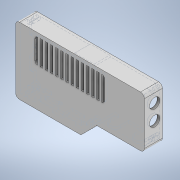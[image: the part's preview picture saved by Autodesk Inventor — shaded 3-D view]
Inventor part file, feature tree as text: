
AUTODESK INVENTOR PART (.ipt)
format: ipt  version: 2021 (Build 250183000, 183)  size: 515,072 bytes
history: native  units: mm
features: sketch x22, extrude x21, chamfer x5, fillet x3, hole x1
ambient origin geometry x8: Origin, YZ Plane, XZ Plane, XY Plane, X Axis, Y Axis, Z Axis, Center Point
bodies: Solid1 (feature_tree)
feature tree (52):
  extrude  "Extrusion1"  Depth=100.0mm
  extrude  "Extrusion3"  Depth=50.0mm
  extrude  "Extrusion4"  Depth=12.5mm
  extrude  "Extrusion12"  Depth=3.0mm TaperAngle=0.0deg
  extrude  "Extrusion13"  Depth=3.0mm TaperAngle=0.0deg
  fillet  "Fillet3"  Radius=2.0mm
  extrude  "Extrusion14"  Depth=2.0mm
  extrude  "Extrusion15"  Depth=44.0mm
  extrude  "Extrusion16"  Depth=12.0mm TaperAngle=0.0deg
  extrude  "Extrusion18"  Depth=12.6mm
  extrude  "Extrusion19"  Depth=3.0mm
  extrude  "Extrusion20"  Depth=1.5mm TaperAngle=0.0deg
  extrude  "Extrusion21"  Depth=4.4mm TaperAngle=0.0deg
  extrude  "Extrusion22"  Depth=2.0mm TaperAngle=0.0deg
  extrude  "Extrusion23"  Depth=14.0mm
  extrude  "Extrusion25"  Depth=4.4mm TaperAngle=0.0deg
  extrude  "Extrusion26"  Depth=4.0mm
  hole  "Hole2"  [1 undecoded]
  chamfer  "Chamfer3"  Distance=12.0mm
  chamfer  "Chamfer4"  Distance=12.0mm
  chamfer  "Chamfer5"  Distance=2.0mm
  chamfer  "Chamfer6"  Distance=8.0mm
  chamfer  "Chamfer7"  Distance=10.0mm
  extrude  "Extrusion27"  Depth=12.0mm
  fillet  "Fillet4"  Radius=8.0mm
  extrude  "Extrusion28"  Depth=8.0mm
  extrude  "Extrusion29"  Depth=8.0mm
  extrude  "Extrusion30"  Depth=2.0mm TaperAngle=0.0deg
  fillet  "Fillet5"  Radius=1.6mm
  extrude  "Extrusion31"  Depth=0.5mm
  sketch  "Sketch1"  dims[d0=52.0mm d1=100.0mm]
  sketch  "Sketch4"  dims[d2=26.0mm d3=50.0mm]
  sketch  "Sketch5"  dims[d4=2.0mm d5=0.0mm d35=12.5mm]
  sketch  "Sketch13"  dims[d36=63.1mm d37=3.0mm d38=0.0mm]
  sketch  "Sketch14"  dims[d39=50.673mm d40=3.0mm d41=0.0mm d79=2.0mm]
  sketch  "Sketch15"  dims[d80=2.0mm d81=2.0mm]
  sketch  "Sketch16"  dims[d82=1.2mm d83=44.0mm]
  sketch  "Sketch17"  dims[d84=59.0mm d85=12.0mm d86=0.0mm]
  sketch  "Sketch19"  dims[d87=2.0mm d88=12.6mm]
  sketch  "Sketch20"  dims[d89=12.0mm d90=0.0mm d91=3.0mm]
  sketch  "Sketch21"  dims[d92=7.8mm d93=1.5mm d94=0.0mm]
  sketch  "Sketch22"  dims[d95=33.8mm d96=4.4mm d97=0.0mm]
  sketch  "Sketch23"  dims[d98=2.0mm d99=2.0mm d100=0.0mm]
  sketch  "Sketch24"  dims[d108=3.0mm d109=14.0mm]
  sketch  "Sketch26"  dims[d110=10.0mm d111=4.4mm d112=0.0mm]
  sketch  "Sketch27"  dims[d113=1.3mm d114=4.0mm]
  sketch  "Sketch28"  dims[d115=3.0mm d116=0.0mm d117=2.0mm]
  sketch  "Sketch29"  dims[d118=2.0mm d119=12.0mm d120=0.0mm d121=12.0mm d122=0.0mm]
  sketch  "Sketch30"  dims[d123=70.0mm]
  sketch  "Sketch31"  dims[d124=89.0mm]
  sketch  "Sketch32"  dims[d125=8.0mm]
  sketch  "Sketch33"  dims[d126=8.0mm d127=2.0mm d128=0.0mm d129=8.0mm d130=10.0mm d131=12.0mm d132=8.0mm d133=8.0mm d134=8.0mm d135=2.0mm d136=0.0mm d140=1.6mm d141=0.5mm d142=9.4mm d143=0.0mm d144=3.0mm d145=3.0mm d146=3.0mm d147=50.0mm d148=97.0mm d149=15.0mm d150=3.0mm d151=3.0mm d152=97.0mm d153=49.0mm d154=4.8mm d155=4.8mm d156=4.8mm d157=4.8mm d158=4.8mm d159=5.0mm d160=0.0mm d161=2.0mm d162=6.0mm d163=4.0mm d164=2.0mm d165=90.0deg d166=4.0mm d167=20.594885mm d168=2.0mm d169=2.0mm d170=45.0deg d171=1.0mm d172=2.0mm d173=45.0deg d174=2.0mm d175=2.0mm d176=45.0deg d177=2.0mm d178=2.0mm d179=45.0deg d180=0.8mm d181=2.0mm d182=45.0deg d184=68.0mm d189=2.0mm d190=0.0mm d191=2.0mm d192=2.0mm d193=24.0mm d194=2.0mm d195=0.0mm d196=36.5mm d197=46.5mm d198=3.5mm d199=2.0mm d200=0.0mm d201=12.5mm d202=23.0mm d203=3.5mm d204=2.0mm d205=0.0mm d206=1.0mm d207=8.0mm d208=1.0mm d209=0.0mm d67=0.5mm d68=0.872665mm d69=0.5mm d70=0.872665mm d71=0.5mm d72=0.872665mm d73=0.5mm d74=0.872665mm d75=0.872665mm d76=0.5mm d77=0.872665mm d210=0.5mm d211=0.872665mm]
note: 1 required parameter value undecoded (feature->parameter linkage not recoverable at this tier; creation-order binding heuristic only, values carry confidence <= 0.55)
